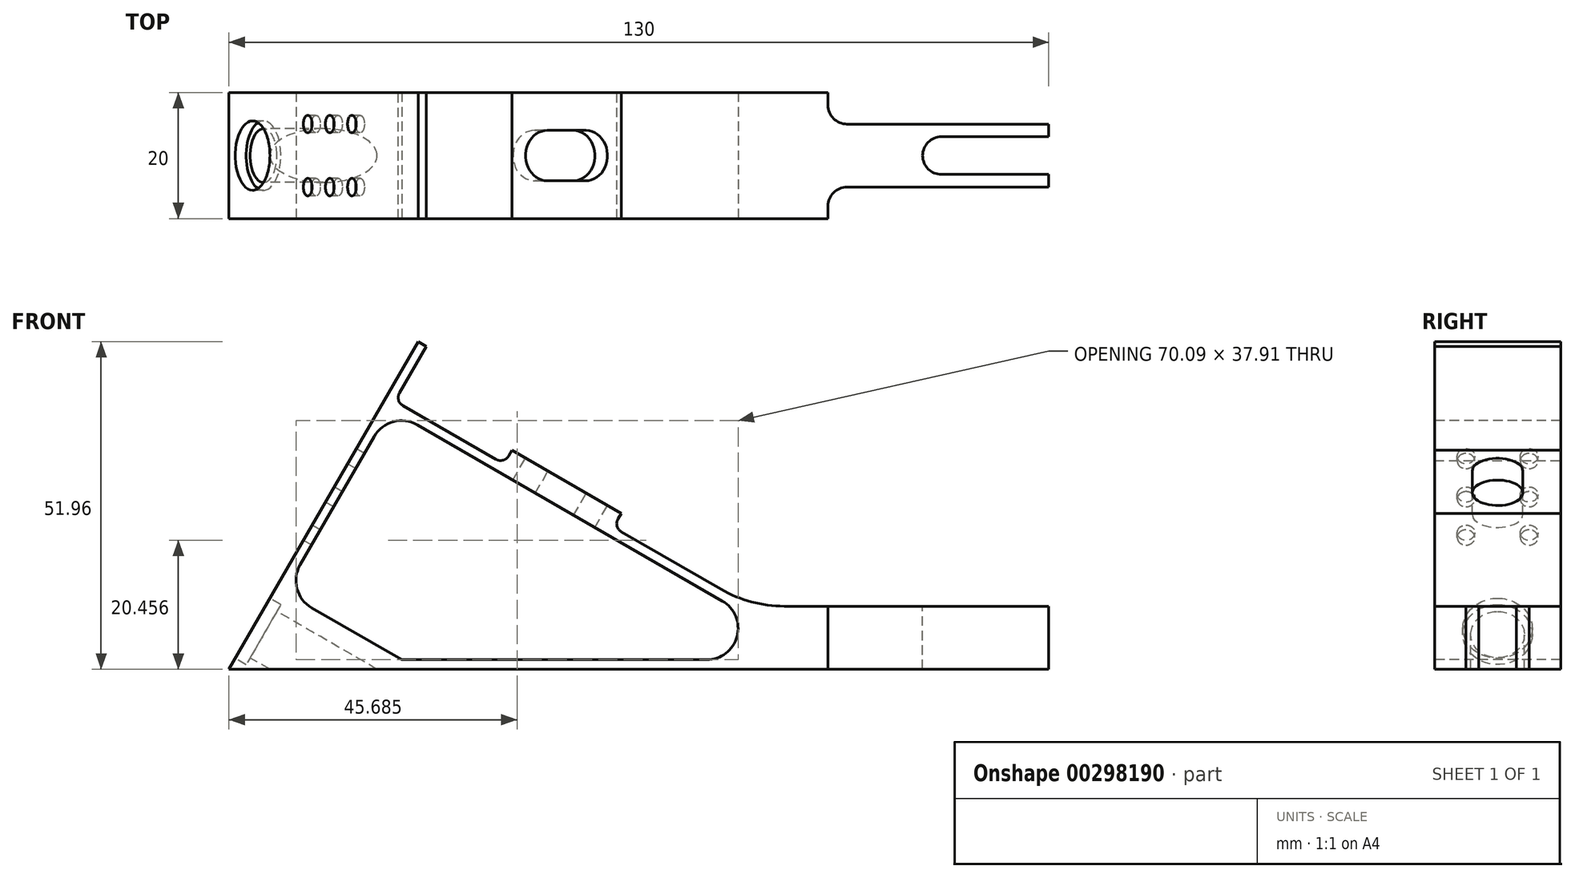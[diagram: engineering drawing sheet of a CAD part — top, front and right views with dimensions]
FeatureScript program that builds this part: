
annotation { "Feature Type Name" : "Feature", "Feature Type Description" : "" }
export const myFeature = defineFeature(function(context is Context, id is Id, definition is map)
    precondition{}
    {
        {
            var Q0;
            Q0=qCreatedBy(makeId("Front.planeOp"),FACE);
            var sketch = newSketch(context, id + "F0", { "sketchPlane" : qUnion([Q0])});
            skLineSegment(sketch, "E0", {"start": v(0, 0) * mm, "end": v(30, 51.96) * mm});
            skLineSegment(sketch, "E1", {"start": v(30, 51.96) * mm, "end": v(31.3, 51.21) * mm});
            skLineSegment(sketch, "E2", {"start": v(31.3, 51.21) * mm, "end": v(26.3, 42.55) * mm});
            skLineSegment(sketch, "E3", {"start": v(26.3, 42.55) * mm, "end": v(43.62, 32.55) * mm});
            skLineSegment(sketch, "E4", {"start": v(43.62, 32.55) * mm, "end": v(44.87, 34.72) * mm});
            skLineSegment(sketch, "E5", {"start": v(44.87, 34.72) * mm, "end": v(62.2, 24.72) * mm});
            skLineSegment(sketch, "E6", {"start": v(62.2, 24.72) * mm, "end": v(60.94, 22.55) * mm});
            skLineSegment(sketch, "E7", {"start": v(60.94, 22.55) * mm, "end": v(82.68, 10) * mm});
            skLineSegment(sketch, "E8", {"start": v(82.68, 10) * mm, "end": v(130, 10) * mm});
            skLineSegment(sketch, "E9", {"start": v(130, 10) * mm, "end": v(130, 0) * mm});
            skLineSegment(sketch, "E10", {"start": v(130, 0) * mm, "end": v(0, 0) * mm});
            skLineSegment(sketch, "E11", {"start": v(27.4, 1.5) * mm, "end": v(75.74, 1.5) * mm});
            skLineSegment(sketch, "E12", {"start": v(78.24, 10.83) * mm, "end": v(29.88, 38.75) * mm});
            skLineSegment(sketch, "E13", {"start": v(27.4, 1.5) * mm, "end": v(13.13, 9.74) * mm});
            skLineSegment(sketch, "E14", {"start": v(11.3, 16.57) * mm, "end": v(23.05, 36.92) * mm});
            skArc(sketch, "E15", {"start": v(29.88, 38.75) * mm, "mid": v(26.09, 39.25) * mm, "end": v(23.05, 36.92) * mm});
            skArc(sketch, "E16", {"start": v(11.3, 16.57) * mm, "mid": v(10.8, 12.78) * mm, "end": v(13.13, 9.74) * mm});
            skArc(sketch, "E17", {"start": v(75.74, 1.5) * mm, "mid": v(80.57, 5.2) * mm, "end": v(78.24, 10.83) * mm});
            skSolve(sketch);
        }
        {
            var Q0;
            Q0 = qSketchRegion(id + "F0", true);
            extrude(context, id + "F1", {"entities" : qUnion([Q0]), "oppositeDirection" : true, "depth" : 20 * mm});
        }
        {
            var Q0;
            Q0=makeQuery(id+"F1.opExtrude","SWEPT_EDGE",EDGE,{"disambiguationData":[OSD([sQuery(id+"F0.wireOp",EDGE,"E6"),sQuery(id+"F0.wireOp",EDGE,"E7")])]});
            var Q1;
            Q1=makeQuery(id+"F1.opExtrude","SWEPT_EDGE",EDGE,{"disambiguationData":[OSD([sQuery(id+"F0.wireOp",EDGE,"E3"),sQuery(id+"F0.wireOp",EDGE,"E4")])]});
            var Q2;
            Q2=makeQuery(id+"F1.opExtrude","SWEPT_EDGE",EDGE,{"disambiguationData":[OSD([sQuery(id+"F0.wireOp",EDGE,"E2"),sQuery(id+"F0.wireOp",EDGE,"E3")])]});
            fillet(context, id + "F2", {"entities" : qUnion([Q0, Q1, Q2]), "radius" : 1.5 * mm, "tangentPropagation" : true, "allowEdgeOverflow" : false});
        }
        {
            var Q0;
            Q0=makeQuery(id+"F1.opExtrude","SWEPT_EDGE",EDGE,{"disambiguationData":[OSD([sQuery(id+"F0.wireOp",EDGE,"E7"),sQuery(id+"F0.wireOp",EDGE,"E8")])]});
            fillet(context, id + "F3", {"entities" : qUnion([Q0]), "radius" : 20 * mm, "tangentPropagation" : true, "allowEdgeOverflow" : false});
        }
        {
            var Q0;
            Q0=makeQuery(id+"F1.opExtrude","SWEPT_FACE",FACE,{"disambiguationData":[OSD([sQuery(id+"F0.wireOp",EDGE,"E8")])]});
            var sketch = newSketch(context, id + "F4", { "sketchPlane" : qUnion([Q0])});
            skLineSegment(sketch, "E18", {"start": v(130, 5) * mm, "end": v(95, 5) * mm});
            skLineSegment(sketch, "E19", {"start": v(130, 15) * mm, "end": v(95, 15) * mm});
            skLineSegment(sketch, "E20", {"start": v(130, 7) * mm, "end": v(113, 7) * mm});
            skLineSegment(sketch, "E21", {"start": v(130, 13) * mm, "end": v(113, 13) * mm});
            skArc(sketch, "E22", {"start": v(113, 13) * mm, "mid": v(110, 10) * mm, "end": v(113, 7) * mm});
            skLineSegment(sketch, "E23", {"start": v(130, 0) * mm, "end": v(130, 20) * mm, "construction": true});
            skLineSegment(sketch, "E24", {"start": v(130, 0) * mm, "end": v(95, 0) * mm});
            skLineSegment(sketch, "E25", {"start": v(130, 20) * mm, "end": v(95, 20) * mm});
            skLineSegment(sketch, "E26", {"start": v(95, 0) * mm, "end": v(95, 5) * mm});
            skLineSegment(sketch, "E27", {"start": v(95, 15) * mm, "end": v(95, 20) * mm});
            skSolve(sketch);
        }
        {
            var Q0;
            {var subQ0=sQuery(id+"F4.wireOp",EDGE,"E18");Q0=makeQuery(id+"F4.imprint","IMPRINT",FACE,{"disambiguationData":[TD([[makeQuery(id+"F4.imprint","IMPRINT",EDGE,{"derivedFrom":subQ0}),1.0]])]});}
            var Q1;
            {var subQ0=sQuery(id+"F4.wireOp",EDGE,"E19");Q1=makeQuery(id+"F4.imprint","IMPRINT",FACE,{"disambiguationData":[TD([[makeQuery(id+"F4.imprint","IMPRINT",EDGE,{"derivedFrom":subQ0}),-1.0]])]});}
            var Q2;
            {var subQ0=sQuery(id+"F4.wireOp",EDGE,"E20");Q2=makeQuery(id+"F4.imprint","IMPRINT",FACE,{"disambiguationData":[TD([[makeQuery(id+"F4.imprint","IMPRINT",EDGE,{"derivedFrom":subQ0}),-1.0]])]});}
            extrude(context, id + "F5", {"entities" : qUnion([Q0, Q1, Q2]), "operationType" : NewBodyOperationType.REMOVE, "endBound" : BoundingType.THROUGH_ALL, "oppositeDirection" : true, "depth" : 25 * mm});
        }
        {
            var Q0;
            Q0=makeQuery(id+"F5.boolean.opBoolean","COPY",EDGE,{"derivedFrom":makeQuery(id+"F5.opExtrude","SWEPT_EDGE",EDGE,{"disambiguationData":[OSD([sQuery(id+"F4.wireOp",EDGE,"E18"),sQuery(id+"F4.wireOp",EDGE,"E26")])]})});
            var Q1;
            Q1=makeQuery(id+"F5.boolean.opBoolean","COPY",EDGE,{"derivedFrom":makeQuery(id+"F5.opExtrude","SWEPT_EDGE",EDGE,{"disambiguationData":[OSD([sQuery(id+"F4.wireOp",EDGE,"E19"),sQuery(id+"F4.wireOp",EDGE,"E27")])]})});
            fillet(context, id + "F6", {"entities" : qUnion([Q0, Q1]), "radius" : 3 * mm, "tangentPropagation" : true, "allowEdgeOverflow" : false});
        }
        {
            var Q0;
            Q0=makeQuery(id+"F1.opExtrude","SWEPT_FACE",FACE,{"disambiguationData":[OSD([sQuery(id+"F0.wireOp",EDGE,"E5")])]});
            var sketch = newSketch(context, id + "F7", { "sketchPlane" : qUnion([Q0])});
            skLineSegment(sketch, "E28", {"start": v(31.5, 0) * mm, "end": v(31.5, 20) * mm});
            skLineSegment(sketch, "E29", {"start": v(28.11, 6) * mm, "end": v(35, 6) * mm});
            skLineSegment(sketch, "E30", {"start": v(28, 14) * mm, "end": v(35.11, 14) * mm});
            skArc(sketch, "E31", {"start": v(28, 14) * mm, "mid": v(24, 9.94) * mm, "end": v(28.11, 6) * mm});
            skArc(sketch, "E32", {"start": v(35, 6) * mm, "mid": v(39, 9.94) * mm, "end": v(35.11, 14) * mm});
            skSolve(sketch);
        }
        {
            var Q0;
            {var subQ5=sQuery(id+"F7.wireOp",EDGE,"E32");Q0=makeQuery(id+"F7.imprint","IMPRINT",FACE,{"disambiguationData":[TD([[makeQuery(id+"F7.imprint","IMPRINT",EDGE,{"derivedFrom":subQ5}),1.0]])]});}
            var Q1;
            {var subQ5=sQuery(id+"F7.wireOp",EDGE,"E31");Q1=makeQuery(id+"F7.imprint","IMPRINT",FACE,{"disambiguationData":[TD([[makeQuery(id+"F7.imprint","IMPRINT",EDGE,{"derivedFrom":subQ5}),1.0]])]});}
            extrude(context, id + "F8", {"entities" : qUnion([Q0, Q1]), "operationType" : NewBodyOperationType.REMOVE, "endBound" : BoundingType.UP_TO_NEXT, "oppositeDirection" : true, "depth" : 4 * mm});
        }
        {
            var Q0;
            Q0=makeQuery(id+"F1.opExtrude","SWEPT_FACE",FACE,{"disambiguationData":[OSD([sQuery(id+"F0.wireOp",EDGE,"E0")])]});
            var sketch = newSketch(context, id + "F9", { "sketchPlane" : qUnion([Q0])});
            skCircle(sketch, "E33", {"center": v(-10, 7.5) * mm, "radius": 4.25 * mm});
            skCircle(sketch, "E34", {"center": v(-15, 25) * mm, "radius": 1.4 * mm});
            skCircle(sketch, "E35", {"center": v(-15, 32) * mm, "radius": 1.4 * mm});
            skCircle(sketch, "E36", {"center": v(-15, 39) * mm, "radius": 1.4 * mm});
            skCircle(sketch, "E37", {"center": v(-5, 25) * mm, "radius": 1.4 * mm});
            skCircle(sketch, "E38", {"center": v(-5, 32) * mm, "radius": 1.4 * mm});
            skCircle(sketch, "E39", {"center": v(-5, 39) * mm, "radius": 1.4 * mm});
            skLineSegment(sketch, "E40", {"start": v(-10, 0) * mm, "end": v(-10, 60) * mm, "construction": true});
            skCircle(sketch, "E41", {"center": v(-10, 7.5) * mm, "radius": 5.5 * mm});
            skSolve(sketch);
        }
        {
            var Q0;
            Q0=makeQuery(id+"F9.imprint","IMPRINT",FACE,{"disambiguationData":[TD([[makeQuery(id+"F9.imprint","IMPRINT",EDGE,{"derivedFrom":sQuery(id+"F9.wireOp",EDGE,"E33")}),-1.0]])]});
            extrude(context, id + "F10", {"entities" : qUnion([Q0]), "operationType" : NewBodyOperationType.REMOVE, "oppositeDirection" : true, "depth" : 2 * mm});
        }
        {
            var Q0;
            Q0=makeQuery(id+"F9.imprint","IMPRINT",FACE,{"disambiguationData":[TD([[makeQuery(id+"F9.imprint","IMPRINT",EDGE,{"derivedFrom":sQuery(id+"F9.wireOp",EDGE,"E36")}),1.0]])]});
            var Q1;
            Q1=makeQuery(id+"F9.imprint","IMPRINT",FACE,{"disambiguationData":[TD([[makeQuery(id+"F9.imprint","IMPRINT",EDGE,{"derivedFrom":sQuery(id+"F9.wireOp",EDGE,"E39")}),1.0]])]});
            var Q2;
            Q2=makeQuery(id+"F9.imprint","IMPRINT",FACE,{"disambiguationData":[TD([[makeQuery(id+"F9.imprint","IMPRINT",EDGE,{"derivedFrom":sQuery(id+"F9.wireOp",EDGE,"E38")}),1.0]])]});
            var Q3;
            Q3=makeQuery(id+"F9.imprint","IMPRINT",FACE,{"disambiguationData":[TD([[makeQuery(id+"F9.imprint","IMPRINT",EDGE,{"derivedFrom":sQuery(id+"F9.wireOp",EDGE,"E37")}),1.0]])]});
            var Q4;
            Q4=makeQuery(id+"F9.imprint","IMPRINT",FACE,{"disambiguationData":[TD([[makeQuery(id+"F9.imprint","IMPRINT",EDGE,{"derivedFrom":sQuery(id+"F9.wireOp",EDGE,"E35")}),1.0]])]});
            var Q5;
            Q5=makeQuery(id+"F9.imprint","IMPRINT",FACE,{"disambiguationData":[TD([[makeQuery(id+"F9.imprint","IMPRINT",EDGE,{"derivedFrom":sQuery(id+"F9.wireOp",EDGE,"E34")}),1.0]])]});
            extrude(context, id + "F11", {"entities" : qUnion([Q0, Q1, Q2, Q3, Q4, Q5]), "operationType" : NewBodyOperationType.REMOVE, "endBound" : BoundingType.UP_TO_NEXT, "oppositeDirection" : true, "depth" : 25 * mm});
        }
        {
            var Q0;
            Q0=makeQuery(id+"F9.imprint","IMPRINT",FACE,{"disambiguationData":[TD([[makeQuery(id+"F9.imprint","IMPRINT",EDGE,{"derivedFrom":sQuery(id+"F9.wireOp",EDGE,"E33")}),1.0]])]});
            extrude(context, id + "F12", {"entities" : qUnion([Q0]), "operationType" : NewBodyOperationType.REMOVE, "endBound" : BoundingType.THROUGH_ALL, "oppositeDirection" : true, "depth" : 25 * mm});
        }
    });
